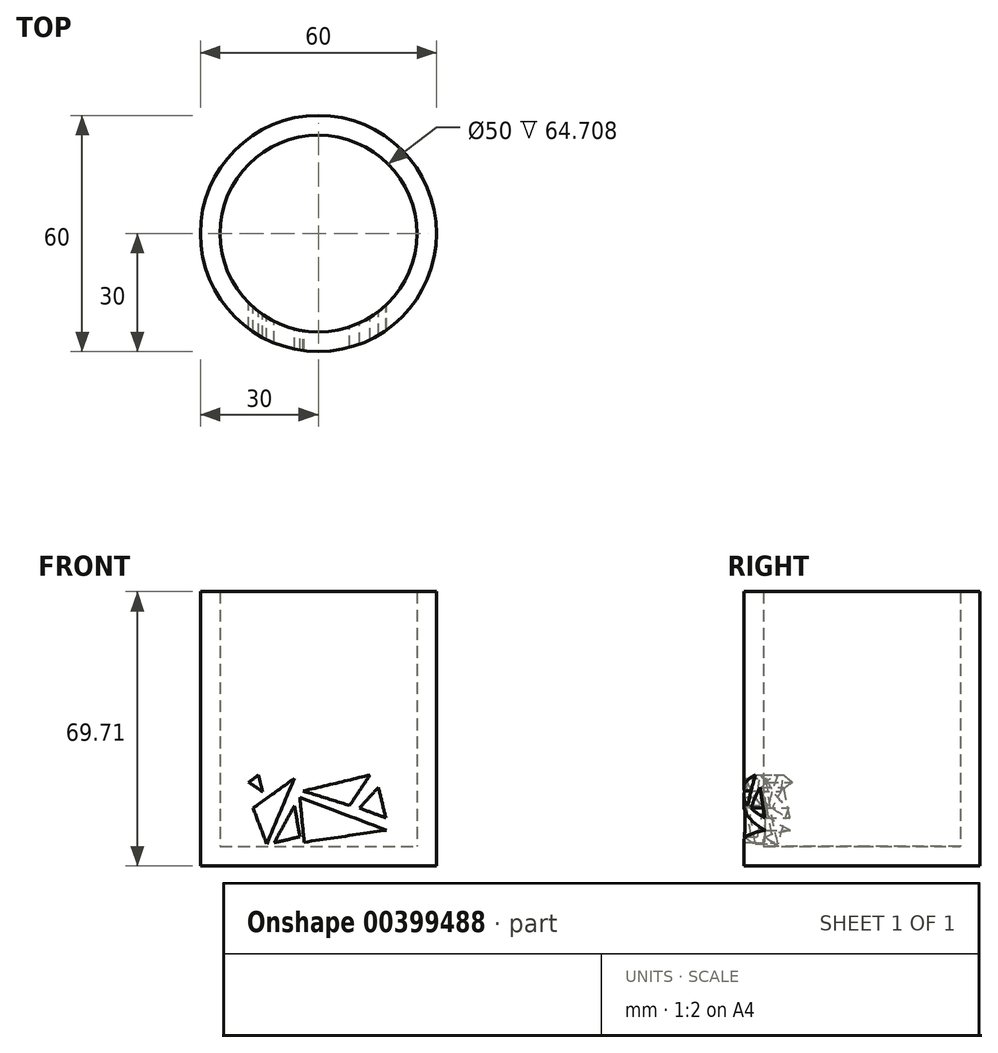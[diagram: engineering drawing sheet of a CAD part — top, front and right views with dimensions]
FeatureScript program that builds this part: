
annotation { "Feature Type Name" : "Feature", "Feature Type Description" : "" }
export const myFeature = defineFeature(function(context is Context, id is Id, definition is map)
    precondition{}
    {
        {
            var Q0;
            Q0=qCreatedBy(makeId("Front.planeOp"),FACE);
            var sketch = newSketch(context, id + "F0", { "sketchPlane" : qUnion([Q0])});
            skLineSegment(sketch, "E0", {"start": v(0, 0) * mm, "end": v(30, 0) * mm});
            skLineSegment(sketch, "E1", {"start": v(30, 0) * mm, "end": v(30, 69.7) * mm});
            skLineSegment(sketch, "E2.0", {"start": v(25, 5) * mm, "end": v(25, 69.7) * mm});
            skLineSegment(sketch, "E2.1", {"start": v(0, 5) * mm, "end": v(25, 5) * mm});
            skLineSegment(sketch, "E3", {"start": v(30, 69.7) * mm, "end": v(25, 69.7) * mm});
            skLineSegment(sketch, "E4", {"start": v(0, 0) * mm, "end": v(0, 5) * mm});
            skSolve(sketch);
        }
        {
            var Q0;
            Q0=makeQuery(id+"F0.imprint","IMPRINT",FACE,{"disambiguationData":[TD([[makeQuery(id+"F0.imprint","IMPRINT",EDGE,{"derivedFrom":sQuery(id+"F0.wireOp",EDGE,"E0")}),1.0]])]});
            var Q1;
            Q1=sQuery(id+"F0.wireOp",EDGE,"E4");
            revolve(context, id + "F1", {"entities" : qUnion([Q0]), "axis" : qUnion([Q1]), "revolveType" : RevolveType.FULL});
        }
        {
            var Q0;
            Q0=qCreatedBy(makeId("Front.planeOp"),FACE);
            var sketch = newSketch(context, id + "F2", { "sketchPlane" : qUnion([Q0])});
            skLineSegment(sketch, "E5.bottom", {"start": v(18.84, 24.23) * mm, "end": v(-18.84, 24.23) * mm, "construction": true});
            skLineSegment(sketch, "E5.top", {"start": v(18.84, 4.23) * mm, "end": v(-18.84, 4.23) * mm, "construction": true});
            skLineSegment(sketch, "E5.left", {"start": v(18.84, 24.23) * mm, "end": v(18.84, 4.23) * mm, "construction": true});
            skLineSegment(sketch, "E5.right", {"start": v(-18.84, 24.23) * mm, "end": v(-18.84, 4.23) * mm, "construction": true});
            skPoint(sketch, "E5.middle", {"position": v(0, 14.23) * mm});
            skLineSegment(sketch, "E6", {"start": v(-6.09, 22.29) * mm, "end": v(-16.62, 14.73) * mm});
            skLineSegment(sketch, "E7", {"start": v(-16.62, 14.73) * mm, "end": v(-13.14, 5.64) * mm});
            skLineSegment(sketch, "E8", {"start": v(-13.14, 5.64) * mm, "end": v(-6.09, 22.29) * mm});
            skLineSegment(sketch, "E9", {"start": v(-4.73, 17.45) * mm, "end": v(-3.63, 6.06) * mm});
            skLineSegment(sketch, "E10", {"start": v(-3.63, 6.06) * mm, "end": v(17.28, 9.12) * mm});
            skLineSegment(sketch, "E11", {"start": v(17.28, 9.12) * mm, "end": v(-4.73, 17.45) * mm});
            skLineSegment(sketch, "E12", {"start": v(15.24, 20) * mm, "end": v(10.4, 14.73) * mm});
            skLineSegment(sketch, "E13", {"start": v(10.4, 14.73) * mm, "end": v(17.1, 12.26) * mm});
            skLineSegment(sketch, "E14", {"start": v(17.1, 12.26) * mm, "end": v(15.24, 20) * mm});
            skLineSegment(sketch, "E15", {"start": v(13.11, 23.14) * mm, "end": v(7.93, 15.4) * mm});
            skLineSegment(sketch, "E16", {"start": v(7.93, 15.4) * mm, "end": v(-3.88, 19.06) * mm});
            skLineSegment(sketch, "E17", {"start": v(-3.88, 19.06) * mm, "end": v(13.11, 23.14) * mm});
            skLineSegment(sketch, "E18", {"start": v(-17.73, 21.27) * mm, "end": v(-14.2, 18.9) * mm});
            skLineSegment(sketch, "E19", {"start": v(-14.2, 18.9) * mm, "end": v(-15.22, 23.14) * mm});
            skLineSegment(sketch, "E20", {"start": v(-15.22, 23.14) * mm, "end": v(-17.73, 21.27) * mm});
            skLineSegment(sketch, "E21", {"start": v(-6.09, 15.32) * mm, "end": v(-11.27, 5.9) * mm});
            skLineSegment(sketch, "E22", {"start": v(-11.27, 5.9) * mm, "end": v(-4.73, 7.46) * mm});
            skLineSegment(sketch, "E23", {"start": v(-4.73, 7.46) * mm, "end": v(-6.09, 15.32) * mm});
            skSolve(sketch);
        }
        {
            var Q0;
            Q0 = qSketchRegion(id + "F2", true);
            extrude(context, id + "F3", {"entities" : qUnion([Q0]), "operationType" : NewBodyOperationType.REMOVE, "endBound" : BoundingType.THROUGH_ALL, "depth" : 25 * mm});
        }
    });
